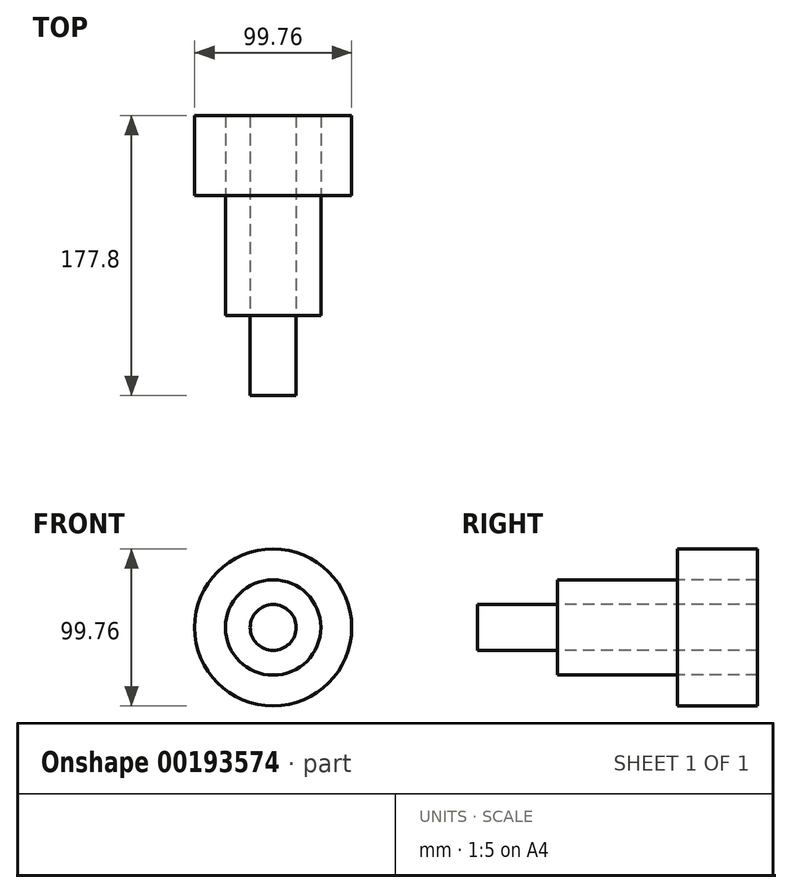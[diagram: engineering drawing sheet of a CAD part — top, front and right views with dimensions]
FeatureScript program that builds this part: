
annotation { "Feature Type Name" : "Feature", "Feature Type Description" : "" }
export const myFeature = defineFeature(function(context is Context, id is Id, definition is map)
    precondition{}
    {
        {
            var Q0;
            Q0=qCreatedBy(makeId("Front.planeOp"),FACE);
            var sketch = newSketch(context, id + "F0", { "sketchPlane" : qUnion([Q0])});
            skCircle(sketch, "E0", {"center": v(0, 0) * mm, "radius": 49.88 * mm});
            skSolve(sketch);
        }
        {
            var Q0;
            Q0=qCreatedBy(makeId("Front.planeOp"),FACE);
            var sketch = newSketch(context, id + "F1", { "sketchPlane" : qUnion([Q0])});
            skCircle(sketch, "E1", {"center": v(0, 0) * mm, "radius": 30.28 * mm});
            skSolve(sketch);
        }
        {
            var Q0;
            Q0=sQuery(id+"F1.wireOp",EDGE,"E1");
            extrude(context, id + "F2", {"bodyType" : ToolBodyType.SURFACE, "surfaceEntities" : qUnion([Q0]), "depth" : 127 * mm});
        }
        {
            var Q0;
            Q0=sQuery(id+"F0.wireOp",EDGE,"E0");
            extrude(context, id + "F3", {"bodyType" : ToolBodyType.SURFACE, "surfaceEntities" : qUnion([Q0]), "depth" : 50.8 * mm});
        }
        {
            var Q0;
            Q0=qCreatedBy(makeId("Front.planeOp"),FACE);
            var sketch = newSketch(context, id + "F4", { "sketchPlane" : qUnion([Q0])});
            skCircle(sketch, "E2", {"center": v(0, 0) * mm, "radius": 14.58 * mm});
            skSolve(sketch);
        }
        {
            var Q0;
            Q0=sQuery(id+"F4.wireOp",EDGE,"E2");
            extrude(context, id + "F5", {"bodyType" : ToolBodyType.SURFACE, "surfaceEntities" : qUnion([Q0]), "depth" : 177.8 * mm});
        }
    });
